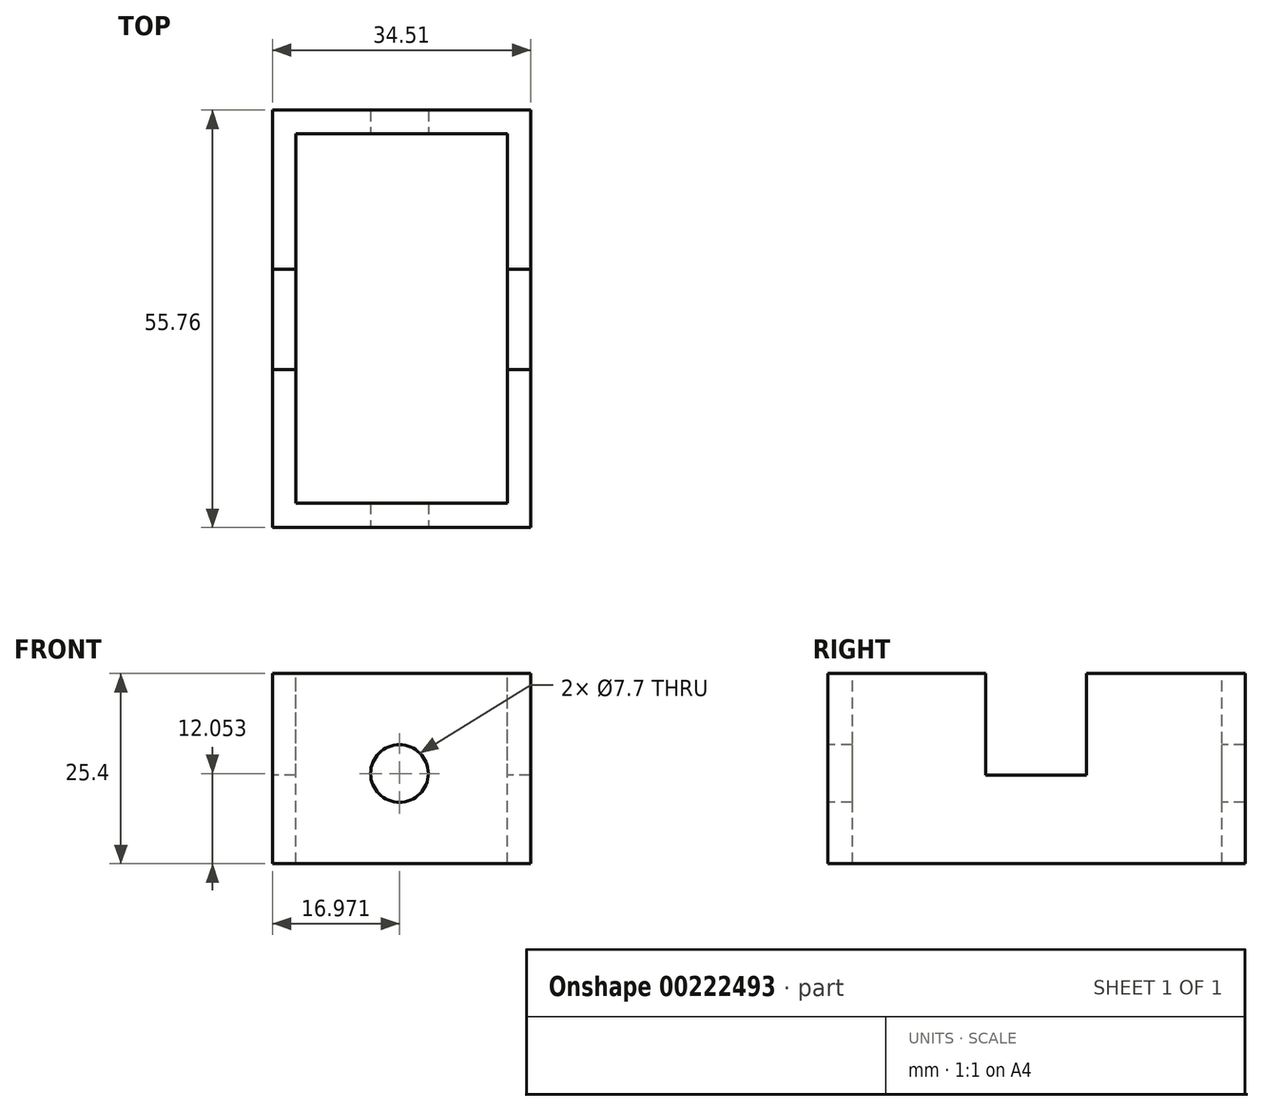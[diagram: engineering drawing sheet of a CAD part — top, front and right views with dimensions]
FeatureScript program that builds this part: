
annotation { "Feature Type Name" : "Feature", "Feature Type Description" : "" }
export const myFeature = defineFeature(function(context is Context, id is Id, definition is map)
    precondition{}
    {
        {
            var Q0;
            Q0=qCreatedBy(makeId("Top.planeOp"),FACE);
            var sketch = newSketch(context, id + "F0", { "sketchPlane" : qUnion([Q0])});
            skLineSegment(sketch, "E0.bottom", {"start": v(0, 0) * mm, "end": v(34.51, 0) * mm});
            skLineSegment(sketch, "E0.top", {"start": v(0, 55.76) * mm, "end": v(34.51, 55.76) * mm});
            skLineSegment(sketch, "E0.left", {"start": v(0, 0) * mm, "end": v(0, 55.76) * mm});
            skLineSegment(sketch, "E0.right", {"start": v(34.51, 0) * mm, "end": v(34.51, 55.76) * mm});
            skSolve(sketch);
        }
        {
            var Q0;
            Q0=makeQuery(id+"F0.imprint","IMPRINT",FACE,{"disambiguationData":[TD([[makeQuery(id+"F0.imprint","IMPRINT",EDGE,{"derivedFrom":sQuery(id+"F0.wireOp",EDGE,"E0.bottom")}),1.0]])]});
            extrude(context, id + "F1", {"entities" : qUnion([Q0]), "depth" : 25.4 * mm});
        }
        {
            var Q0;
            Q0=makeQuery(id+"F1.opExtrude","SWEPT_FACE",FACE,{"disambiguationData":[OSD([sQuery(id+"F0.wireOp",EDGE,"E0.bottom")])]});
            var sketch = newSketch(context, id + "F2", { "sketchPlane" : qUnion([Q0])});
            skCircle(sketch, "E1", {"center": v(16.97, 12.05) * mm, "radius": 3.85 * mm});
            skSolve(sketch);
        }
        {
            var Q0;
            Q0=makeQuery(id+"F2.imprint","IMPRINT",FACE,{"disambiguationData":[TD([[makeQuery(id+"F2.imprint","IMPRINT",EDGE,{"derivedFrom":sQuery(id+"F2.wireOp",EDGE,"E1")}),1.0]])]});
            extrude(context, id + "F3", {"entities" : qUnion([Q0]), "operationType" : NewBodyOperationType.REMOVE, "endBound" : BoundingType.THROUGH_ALL, "oppositeDirection" : true, "depth" : 25.4 * mm});
        }
        {
            var Q0;
            Q0=makeQuery(id+"F1.opExtrude","CAP_FACE",FACE,{"disambiguationData":[OSD([sQuery(id+"F0.wireOp",EDGE,"E0.bottom"),sQuery(id+"F0.wireOp",EDGE,"E0.top"),sQuery(id+"F0.wireOp",EDGE,"E0.left"),sQuery(id+"F0.wireOp",EDGE,"E0.right")])],"isStart":false});
            var sketch = newSketch(context, id + "F4", { "sketchPlane" : qUnion([Q0])});
            skLineSegment(sketch, "E2.bottom", {"start": v(3.14, 3.28) * mm, "end": v(31.38, 3.28) * mm});
            skLineSegment(sketch, "E2.top", {"start": v(3.14, 52.63) * mm, "end": v(31.38, 52.63) * mm});
            skLineSegment(sketch, "E2.left", {"start": v(3.14, 3.28) * mm, "end": v(3.14, 52.63) * mm});
            skLineSegment(sketch, "E2.right", {"start": v(31.38, 3.28) * mm, "end": v(31.38, 52.63) * mm});
            skSolve(sketch);
        }
        {
            var Q0;
            Q0=makeQuery(id+"F4.imprint","IMPRINT",FACE,{"disambiguationData":[TD([[makeQuery(id+"F4.imprint","IMPRINT",EDGE,{"derivedFrom":sQuery(id+"F4.wireOp",EDGE,"E2.bottom")}),1.0]])]});
            extrude(context, id + "F5", {"entities" : qUnion([Q0]), "operationType" : NewBodyOperationType.REMOVE, "endBound" : BoundingType.THROUGH_ALL, "oppositeDirection" : true, "depth" : 25.4 * mm});
        }
        {
            var Q0;
            Q0=makeQuery(id+"F1.opExtrude","SWEPT_FACE",FACE,{"disambiguationData":[OSD([sQuery(id+"F0.wireOp",EDGE,"E0.left")])]});
            var sketch = newSketch(context, id + "F6", { "sketchPlane" : qUnion([Q0])});
            skLineSegment(sketch, "E3", {"start": v(-34.51, 25.4) * mm, "end": v(-34.51, 11.84) * mm});
            skLineSegment(sketch, "E4", {"start": v(-34.51, 11.84) * mm, "end": v(-21.1, 11.84) * mm});
            skLineSegment(sketch, "E5", {"start": v(-21.1, 25.4) * mm, "end": v(-21.1, 11.84) * mm});
            skLineSegment(sketch, "E6", {"start": v(-21.1, 25.4) * mm, "end": v(-34.51, 25.4) * mm});
            skLineSegment(sketch, "E7", {"start": v(-34.51, 25.4) * mm, "end": v(-21.1, 25.4) * mm});
            skSolve(sketch);
        }
        {
            var Q0;
            Q0=makeQuery(id+"F6.imprint","IMPRINT",FACE,{"disambiguationData":[TD([[makeQuery(id+"F6.imprint","IMPRINT",EDGE,{"derivedFrom":sQuery(id+"F6.wireOp",EDGE,"E3")}),1.0]])]});
            extrude(context, id + "F7", {"entities" : qUnion([Q0]), "operationType" : NewBodyOperationType.REMOVE, "endBound" : BoundingType.THROUGH_ALL, "oppositeDirection" : true, "depth" : 25.4 * mm});
        }
    });
